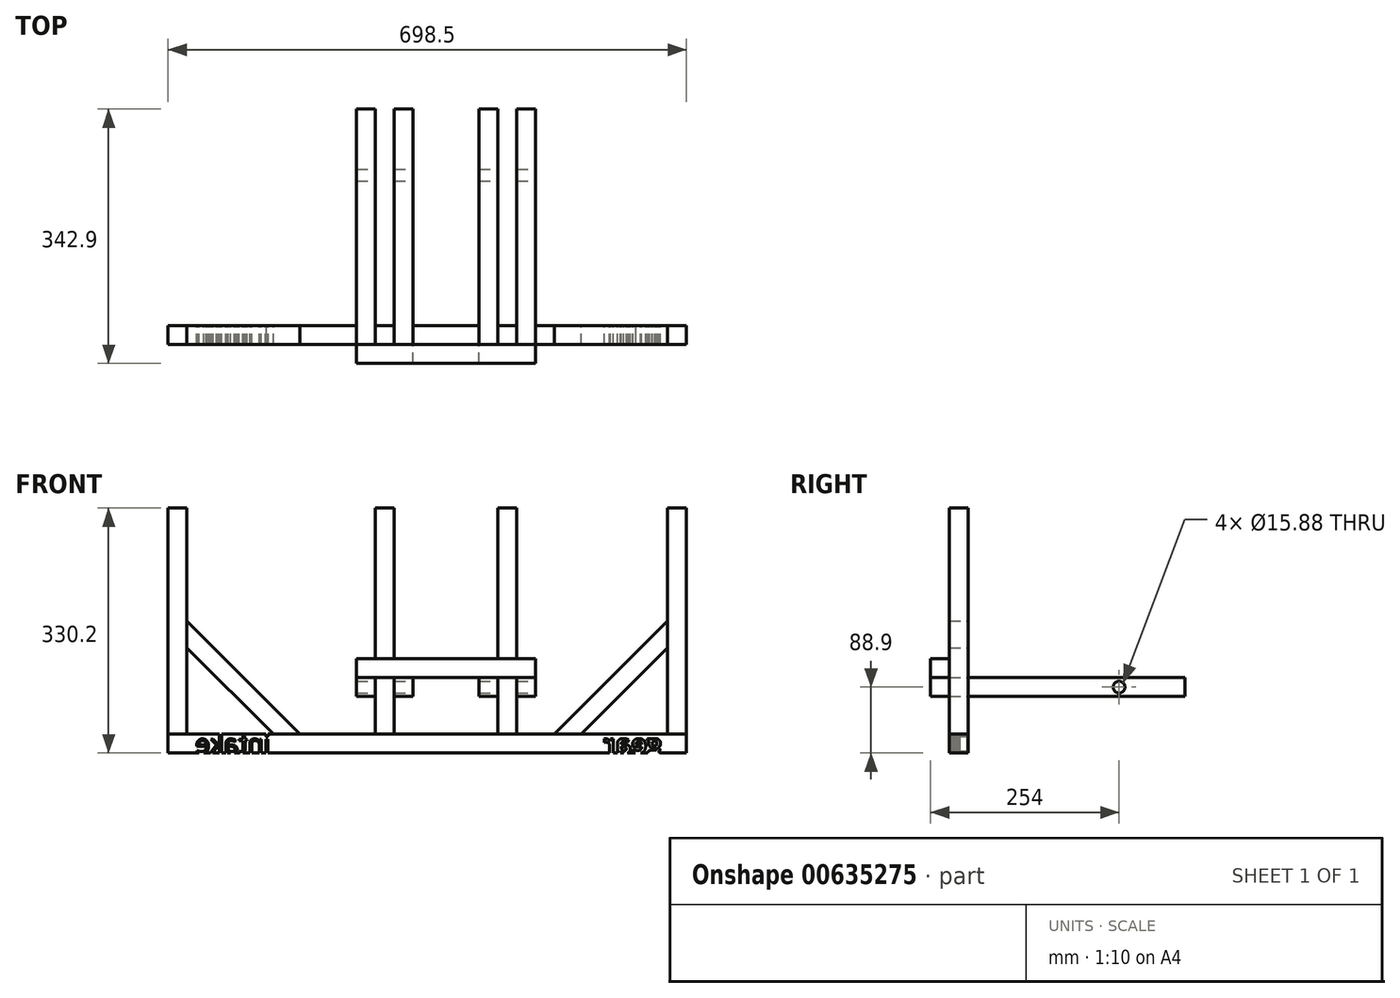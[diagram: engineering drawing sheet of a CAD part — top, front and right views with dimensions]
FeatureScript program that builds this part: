
annotation { "Feature Type Name" : "Feature", "Feature Type Description" : "" }
export const myFeature = defineFeature(function(context is Context, id is Id, definition is map)
    precondition{}
    {
        {
            assignVariable(context, id + "F0", {"name" : "beamLength", "anyValue" : 304.8 * mm});
        }
        {
            assignVariable(context, id + "F1", {"name" : "framePieceLength", "anyValue" : 304.8 * mm});
        }
        {
            assignVariable(context, id + "F2", {"name" : "alumEdge", "anyValue" : 25.4 * mm});
        }
        {
            var Q0;
            Q0=qCreatedBy(makeId("Top.planeOp"),FACE);
            var sketch = newSketch(context, id + "F3", { "sketchPlane" : qUnion([Q0])});
            skLineSegment(sketch, "E0.bottom", {"start": v(-349.25, 12.7) * mm, "end": v(-323.85, 12.7) * mm});
            skLineSegment(sketch, "E0.top", {"start": v(-349.25, -12.7) * mm, "end": v(-323.85, -12.7) * mm});
            skLineSegment(sketch, "E0.left", {"start": v(-349.25, 12.7) * mm, "end": v(-349.25, -12.7) * mm});
            skLineSegment(sketch, "E0.right", {"start": v(-323.85, 12.7) * mm, "end": v(-323.85, -12.7) * mm});
            skPoint(sketch, "E0.middle", {"position": v(-336.55, 0) * mm});
            skLineSegment(sketch, "E1.bottom", {"start": v(349.25, 12.7) * mm, "end": v(323.85, 12.7) * mm});
            skLineSegment(sketch, "E1.top", {"start": v(349.25, -12.7) * mm, "end": v(323.85, -12.7) * mm});
            skLineSegment(sketch, "E1.left", {"start": v(349.25, 12.7) * mm, "end": v(349.25, -12.7) * mm});
            skLineSegment(sketch, "E1.right", {"start": v(323.85, 12.7) * mm, "end": v(323.85, -12.7) * mm});
            skPoint(sketch, "E1.middle", {"position": v(336.55, 0) * mm});
            skLineSegment(sketch, "E2", {"start": v(-349.25, 0) * mm, "end": v(349.25, 0) * mm, "construction": true});
            skLineSegment(sketch, "E3.bottom", {"start": v(120.65, 12.7) * mm, "end": v(95.25, 12.7) * mm});
            skLineSegment(sketch, "E3.top", {"start": v(120.65, -12.7) * mm, "end": v(95.25, -12.7) * mm});
            skLineSegment(sketch, "E3.left", {"start": v(120.65, 12.7) * mm, "end": v(120.65, -12.7) * mm});
            skLineSegment(sketch, "E3.right", {"start": v(95.25, 12.7) * mm, "end": v(95.25, -12.7) * mm});
            skPoint(sketch, "E3.middle", {"position": v(107.95, 0) * mm});
            skLineSegment(sketch, "E4.bottom", {"start": v(-44.45, 12.7) * mm, "end": v(-69.85, 12.7) * mm});
            skLineSegment(sketch, "E4.top", {"start": v(-44.45, -12.7) * mm, "end": v(-69.85, -12.7) * mm});
            skLineSegment(sketch, "E4.left", {"start": v(-44.45, 12.7) * mm, "end": v(-44.45, -12.7) * mm});
            skLineSegment(sketch, "E4.right", {"start": v(-69.85, 12.7) * mm, "end": v(-69.85, -12.7) * mm});
            skPoint(sketch, "E4.middle", {"position": v(-57.15, 0) * mm});
            skPoint(sketch, "E4.cornerSnap0", {"position": v(107.95, 12.7) * mm});
            skSolve(sketch);
        }
        {
            var Q0;
            Q0=makeQuery(id+"F3.imprint","IMPRINT",FACE,{"disambiguationData":[TD([[makeQuery(id+"F3.imprint","IMPRINT",EDGE,{"derivedFrom":sQuery(id+"F3.wireOp",EDGE,"E0.bottom")}),-1.0]])]});
            var Q1;
            Q1=makeQuery(id+"F3.imprint","IMPRINT",FACE,{"disambiguationData":[TD([[makeQuery(id+"F3.imprint","IMPRINT",EDGE,{"derivedFrom":sQuery(id+"F3.wireOp",EDGE,"E4.bottom")}),1.0]])]});
            var Q2;
            Q2=makeQuery(id+"F3.imprint","IMPRINT",FACE,{"disambiguationData":[TD([[makeQuery(id+"F3.imprint","IMPRINT",EDGE,{"derivedFrom":sQuery(id+"F3.wireOp",EDGE,"E3.bottom")}),1.0]])]});
            var Q3;
            Q3=makeQuery(id+"F3.imprint","IMPRINT",FACE,{"disambiguationData":[TD([[makeQuery(id+"F3.imprint","IMPRINT",EDGE,{"derivedFrom":sQuery(id+"F3.wireOp",EDGE,"E1.bottom")}),1.0]])]});
            extrude(context, id + "F4", {"entities" : qUnion([Q0, Q1, Q2, Q3]), "depth" : getVariable(context, 'framePieceLength'), "offsetDistance" : 25 * mm});
        }
        {
            var Q0;
            Q0=qCreatedBy(makeId("Front.planeOp"),FACE);
            var sketch = newSketch(context, id + "F5", { "sketchPlane" : qUnion([Q0])});
            skLineSegment(sketch, "E5.bottom", {"start": v(349.25, 0) * mm, "end": v(-349.25, 0) * mm});
            skLineSegment(sketch, "E5.top", {"start": v(349.25, -25.4) * mm, "end": v(-349.25, -25.4) * mm});
            skLineSegment(sketch, "E5.left", {"start": v(349.25, 0) * mm, "end": v(349.25, -25.4) * mm});
            skLineSegment(sketch, "E5.right", {"start": v(-349.25, 0) * mm, "end": v(-349.25, -25.4) * mm});
            skSolve(sketch);
        }
        {
            var Q0;
            Q0=makeQuery(id+"F5.imprint","IMPRINT",FACE,{"disambiguationData":[TD([[makeQuery(id+"F5.imprint","IMPRINT",EDGE,{"derivedFrom":sQuery(id+"F5.wireOp",EDGE,"E5.bottom")}),1.0]])]});
            extrude(context, id + "F6", {"entities" : qUnion([Q0]), "depth" : getVariable(context, 'alumEdge'), "offsetDistance" : 25 * mm, "symmetric" : true});
        }
        {
            var Q0;
            Q0=makeQuery(id+"F6.opExtrude","CAP_FACE",FACE,{"disambiguationData":[OSD([sQuery(id+"F5.wireOp",EDGE,"E5.bottom"),sQuery(id+"F5.wireOp",EDGE,"E5.top"),sQuery(id+"F5.wireOp",EDGE,"E5.left"),sQuery(id+"F5.wireOp",EDGE,"E5.right")])],"isStart":true});
            var sketch = newSketch(context, id + "F7", { "sketchPlane" : qUnion([Q0])});
            skText(sketch, "E6", { "text": "gear", "fontName": "OpenSans-Bold.ttf"});
            skText(sketch, "E7", { "text": "intake", "fontName": "OpenSans-Regular.ttf"});
            const initialGuessF7  = {"E6": [-0.31566, -0.0254, 1, 0, 0.0254], "E7": [0.21161, -0.0254, 1, 0, 0.0254]};
            skSetInitialGuess(sketch, initialGuessF7);
            skSolve(sketch);
        }
        {
            var Q0;
            Q0 = qSketchRegion(id + "F7", true);
            extrude(context, id + "F8", {"entities" : qUnion([Q0]), "operationType" : NewBodyOperationType.REMOVE, "endBound" : BoundingType.THROUGH_ALL, "oppositeDirection" : true, "depth" : getVariable(context, 'alumEdge'), "offsetDistance" : 25 * mm});
        }
        {
            var Q0;
            Q0=qCreatedBy(makeId("Front.planeOp"),FACE);
            var sketch = newSketch(context, id + "F9", { "sketchPlane" : qUnion([Q0])});
            skLineSegment(sketch, "E8", {"start": v(349.25, 8.04) * mm, "end": v(171.45, 8.04) * mm, "construction": true});
            skLineSegment(sketch, "E9", {"start": v(171.45, 0) * mm, "end": v(323.85, 152.4) * mm});
            skLineSegment(sketch, "E10", {"start": v(311.93, 152.4) * mm, "end": v(311.93, -25.4) * mm, "construction": true});
            skLineSegment(sketch, "E11", {"start": v(311.93, 152.4) * mm, "end": v(335.77, 152.4) * mm, "construction": true});
            skPoint(sketch, "E12", {"position": v(323.85, 152.4) * mm});
            skLineSegment(sketch, "E13", {"start": v(207.37, 0) * mm, "end": v(323.85, 116.48) * mm});
            skLineSegment(sketch, "E14", {"start": v(-349.25, 9.12) * mm, "end": v(-171.45, 9.12) * mm, "construction": true});
            skLineSegment(sketch, "E15", {"start": v(-315.1, 152.4) * mm, "end": v(-315.1, -25.4) * mm, "construction": true});
            skLineSegment(sketch, "E16", {"start": v(-171.45, 0) * mm, "end": v(-323.85, 152.4) * mm});
            skLineSegment(sketch, "E17", {"start": v(-323.85, 116.48) * mm, "end": v(-207.37, 0) * mm});
            skLineSegment(sketch, "E18", {"start": v(-323.85, 152.4) * mm, "end": v(-323.85, 116.48) * mm});
            skLineSegment(sketch, "E19", {"start": v(-207.37, 0) * mm, "end": v(-171.45, 0) * mm});
            skLineSegment(sketch, "E20", {"start": v(207.37, 0) * mm, "end": v(171.45, 0) * mm});
            skLineSegment(sketch, "E21", {"start": v(323.85, 152.4) * mm, "end": v(323.85, 116.48) * mm});
            skSolve(sketch);
        }
        {
            var Q0;
            Q0 = qSketchRegion(id + "F9", true);
            extrude(context, id + "F10", {"entities" : qUnion([Q0]), "depth" : getVariable(context, 'alumEdge'), "offsetDistance" : 25 * mm, "symmetric" : true});
        }
        {
            var Q0;
            Q0=qCreatedBy(makeId("Front.planeOp"),FACE);
            var sketch = newSketch(context, id + "F11", { "sketchPlane" : qUnion([Q0])});
            skLineSegment(sketch, "E22", {"start": v(164.46, 50.8) * mm, "end": v(-93.34, 50.8) * mm, "construction": true});
            skLineSegment(sketch, "E23.bottom", {"start": v(120.65, 50.8) * mm, "end": v(146.05, 50.8) * mm});
            skLineSegment(sketch, "E23.top", {"start": v(120.65, 76.2) * mm, "end": v(146.05, 76.2) * mm});
            skLineSegment(sketch, "E23.left", {"start": v(120.65, 50.8) * mm, "end": v(120.65, 76.2) * mm});
            skLineSegment(sketch, "E23.right", {"start": v(146.05, 50.8) * mm, "end": v(146.05, 76.2) * mm});
            skLineSegment(sketch, "E24.bottom", {"start": v(95.25, 50.8) * mm, "end": v(69.85, 50.8) * mm});
            skLineSegment(sketch, "E24.top", {"start": v(95.25, 76.2) * mm, "end": v(69.85, 76.2) * mm});
            skLineSegment(sketch, "E24.left", {"start": v(95.25, 50.8) * mm, "end": v(95.25, 76.2) * mm});
            skLineSegment(sketch, "E24.right", {"start": v(69.85, 50.8) * mm, "end": v(69.85, 76.2) * mm});
            skLineSegment(sketch, "E25.bottom", {"start": v(-44.45, 50.8) * mm, "end": v(-19.05, 50.8) * mm});
            skLineSegment(sketch, "E25.top", {"start": v(-44.45, 76.2) * mm, "end": v(-19.05, 76.2) * mm});
            skLineSegment(sketch, "E25.left", {"start": v(-44.45, 50.8) * mm, "end": v(-44.45, 76.2) * mm});
            skLineSegment(sketch, "E25.right", {"start": v(-19.05, 50.8) * mm, "end": v(-19.05, 76.2) * mm});
            skLineSegment(sketch, "E26.bottom", {"start": v(-69.85, 50.8) * mm, "end": v(-95.25, 50.8) * mm});
            skLineSegment(sketch, "E26.top", {"start": v(-69.85, 76.2) * mm, "end": v(-95.25, 76.2) * mm});
            skLineSegment(sketch, "E26.left", {"start": v(-69.85, 50.8) * mm, "end": v(-69.85, 76.2) * mm});
            skLineSegment(sketch, "E26.right", {"start": v(-95.25, 50.8) * mm, "end": v(-95.25, 76.2) * mm});
            skSolve(sketch);
        }
        {
            var Q0;
            Q0=makeQuery(id+"F11.imprint","IMPRINT",FACE,{"disambiguationData":[TD([[makeQuery(id+"F11.imprint","IMPRINT",EDGE,{"derivedFrom":sQuery(id+"F11.wireOp",EDGE,"E23.bottom")}),1.0]])]});
            var Q1;
            Q1=makeQuery(id+"F11.imprint","IMPRINT",FACE,{"disambiguationData":[TD([[makeQuery(id+"F11.imprint","IMPRINT",EDGE,{"derivedFrom":sQuery(id+"F11.wireOp",EDGE,"E24.bottom")}),-1.0]])]});
            var Q2;
            Q2=makeQuery(id+"F11.imprint","IMPRINT",FACE,{"disambiguationData":[TD([[makeQuery(id+"F11.imprint","IMPRINT",EDGE,{"derivedFrom":sQuery(id+"F11.wireOp",EDGE,"E25.bottom")}),1.0]])]});
            var Q3;
            Q3=makeQuery(id+"F11.imprint","IMPRINT",FACE,{"disambiguationData":[TD([[makeQuery(id+"F11.imprint","IMPRINT",EDGE,{"derivedFrom":sQuery(id+"F11.wireOp",EDGE,"E26.bottom")}),-1.0]])]});
            var Q4;
            Q4 = qConstructionFilter(qBodyType(qCreatedBy(id + "F11" ,EDGE), BodyType.WIRE), ConstructionObject.NO);
            extrude(context, id + "F12", {"entities" : qUnion([Q0, Q1, Q2, Q3]), "surfaceEntities" : qUnion([Q4]), "depth" : getVariable(context, 'alumEdge') * 1.5, "offsetDistance" : 25 * mm, "hasSecondDirection" : true, "secondDirectionOppositeDirection" : true, "secondDirectionDepth" : getVariable(context, 'beamLength')});
        }
        {
            var Q0;
            Q0=makeQuery(id+"F12.opExtrude","SWEPT_FACE",FACE,{"disambiguationData":[OSD([sQuery(id+"F11.wireOp",EDGE,"E25.top")])]});
            var sketch = newSketch(context, id + "F13", { "sketchPlane" : qUnion([Q0])});
            skLineSegment(sketch, "E27.bottom", {"start": v(-95.25, -12.7) * mm, "end": v(146.05, -12.7) * mm});
            skLineSegment(sketch, "E27.top", {"start": v(-95.25, -38.1) * mm, "end": v(146.05, -38.1) * mm});
            skLineSegment(sketch, "E27.left", {"start": v(-95.25, -12.7) * mm, "end": v(-95.25, -38.1) * mm});
            skLineSegment(sketch, "E27.right", {"start": v(146.05, -12.7) * mm, "end": v(146.05, -38.1) * mm});
            skSolve(sketch);
        }
        {
            var Q0;
            Q0 = qSketchRegion(id + "F13", true);
            extrude(context, id + "F14", {"entities" : qUnion([Q0]), "depth" : getVariable(context, 'alumEdge'), "offsetDistance" : 25 * mm});
        }
        {
            var Q0;
            Q0=makeQuery(id+"F12.opExtrude","SWEPT_FACE",FACE,{"disambiguationData":[OSD([sQuery(id+"F11.wireOp",EDGE,"E23.right")])]});
            var sketch = newSketch(context, id + "F15", { "sketchPlane" : qUnion([Q0])});
            skLineSegment(sketch, "E28", {"start": v(12.7, 63.5) * mm, "end": v(215.9, 63.5) * mm, "construction": true});
            skLineSegment(sketch, "E29", {"start": v(75.48, 76.2) * mm, "end": v(75.48, 50.8) * mm, "construction": true});
            skPoint(sketch, "E30", {"position": v(75.48, 63.5) * mm});
            skCircle(sketch, "E31", {"center": v(215.9, 63.5) * mm, "radius": 7.94 * mm});
            skSolve(sketch);
        }
        {
            var Q0;
            Q0=makeQuery(id+"F15.imprint","IMPRINT",FACE,{"disambiguationData":[TD([[makeQuery(id+"F15.imprint","IMPRINT",EDGE,{"derivedFrom":sQuery(id+"F15.wireOp",EDGE,"E31")}),1.0]])]});
            extrude(context, id + "F16", {"entities" : qUnion([Q0]), "operationType" : NewBodyOperationType.REMOVE, "endBound" : BoundingType.THROUGH_ALL, "oppositeDirection" : true, "depth" : 508 * mm, "offsetDistance" : 25 * mm});
        }
    });
